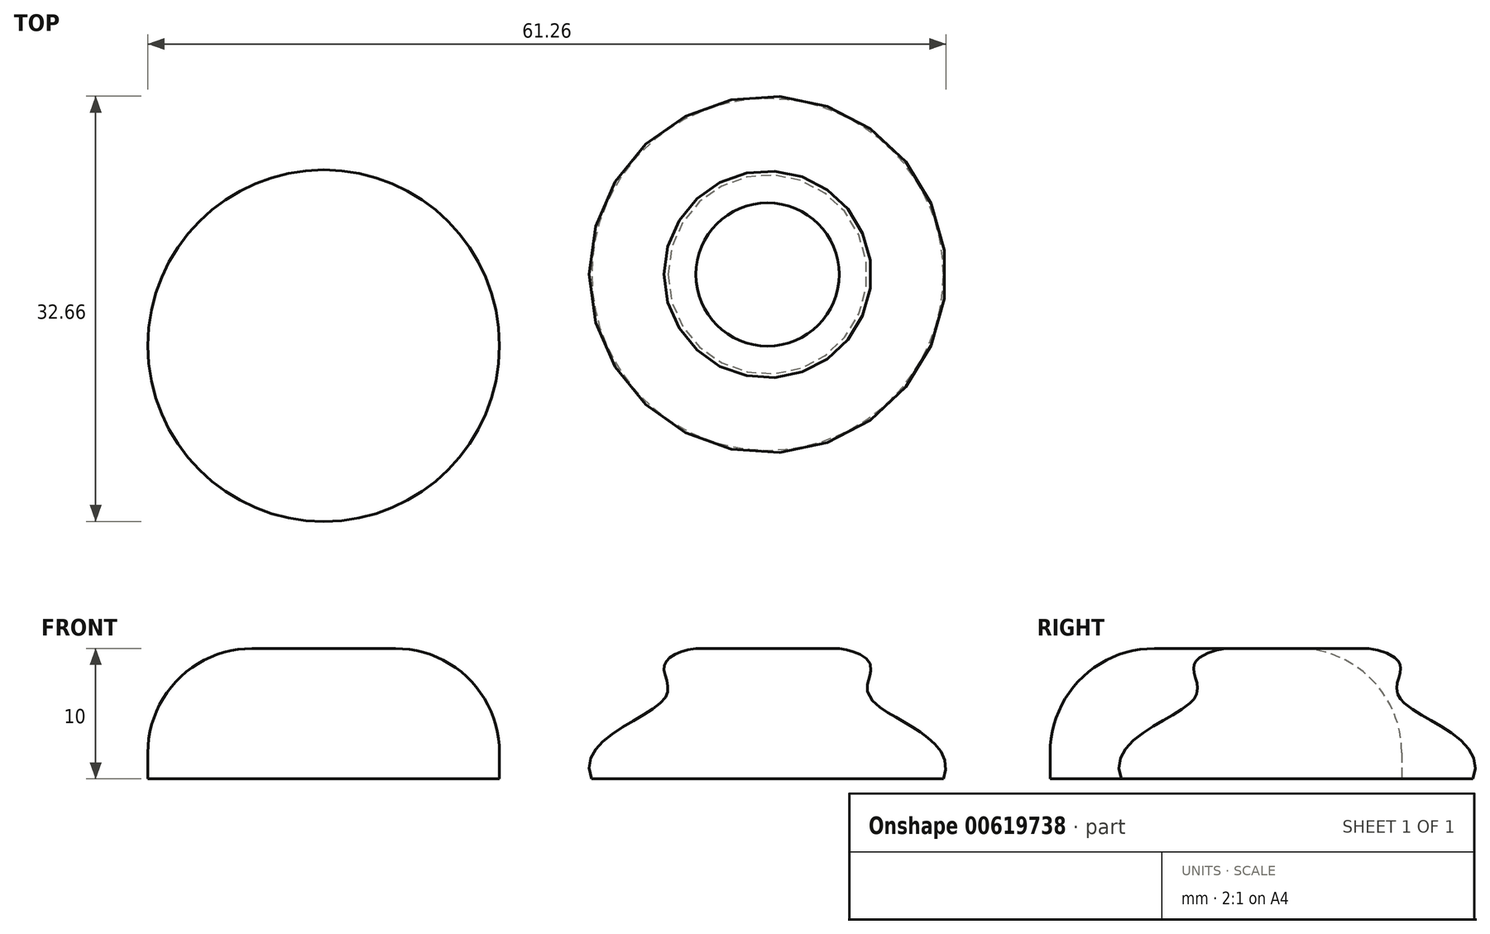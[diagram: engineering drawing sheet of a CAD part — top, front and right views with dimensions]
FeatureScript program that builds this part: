
annotation { "Feature Type Name" : "Feature", "Feature Type Description" : "" }
export const myFeature = defineFeature(function(context is Context, id is Id, definition is map)
    precondition{}
    {
        {
            var Q0;
            Q0=qCreatedBy(makeId("Front.planeOp"),FACE);
            var sketch = newSketch(context, id + "F0", { "sketchPlane" : qUnion([Q0])});
            skLineSegment(sketch, "E0", {"start": v(0, 0) * mm, "end": v(13.5, 0) * mm});
            skLineSegment(sketch, "E1", {"start": v(0, 0) * mm, "end": v(0, 10) * mm});
            skLineSegment(sketch, "E2", {"start": v(0, 10) * mm, "end": v(5.5, 10) * mm});
            skFitSpline(sketch, "E3", {"points": [v(5.5, 10) * mm, v(7.95, 8.6) * mm, v(7.88, 6.17) * mm, v(13.5, 0) * mm], "startDerivative": vector(14.2, -1.86) * mm, "endDerivative": vector(-8.32, -19.87) * mm});
            skSolve(sketch);
        }
        {
            var Q0;
            Q0=qCreatedBy(makeId("Top.planeOp"),FACE);
            var sketch = newSketch(context, id + "F1", { "sketchPlane" : qUnion([Q0])});
            skCircle(sketch, "E4", {"center": v(-34.07, -5.47) * mm, "radius": 13.5 * mm});
            skSolve(sketch);
        }
        {
            var Q0;
            Q0=makeQuery(id+"F1.imprint","IMPRINT",FACE,{"disambiguationData":[TD([[makeQuery(id+"F1.imprint","IMPRINT",EDGE,{"derivedFrom":sQuery(id+"F1.wireOp",EDGE,"E4")}),1.0]])]});
            extrude(context, id + "F2", {"entities" : qUnion([Q0]), "depth" : 10 * mm, "offsetDistance" : 25 * mm});
        }
        {
            var Q0;
            Q0=makeQuery(id+"F2.opExtrude","CAP_EDGE",EDGE,{"disambiguationData":[OSD([sQuery(id+"F1.wireOp",EDGE,"E4")])],"isStart":false});
            fillet(context, id + "F3", {"entities" : qUnion([Q0]), "radius" : 8 * mm, "tangentPropagation" : true, "allowEdgeOverflow" : false});
        }
        {
            var Q0;
            Q0=makeQuery(id+"F0.imprint","IMPRINT",FACE,{"disambiguationData":[TD([[makeQuery(id+"F0.imprint","IMPRINT",EDGE,{"derivedFrom":sQuery(id+"F0.wireOp",EDGE,"E0")}),1.0]])]});
            var Q1;
            Q1=sQuery(id+"F0.wireOp",EDGE,"E1");
            revolve(context, id + "F4", {"entities" : qUnion([Q0]), "axis" : qUnion([Q1]), "revolveType" : RevolveType.FULL});
        }
    });
